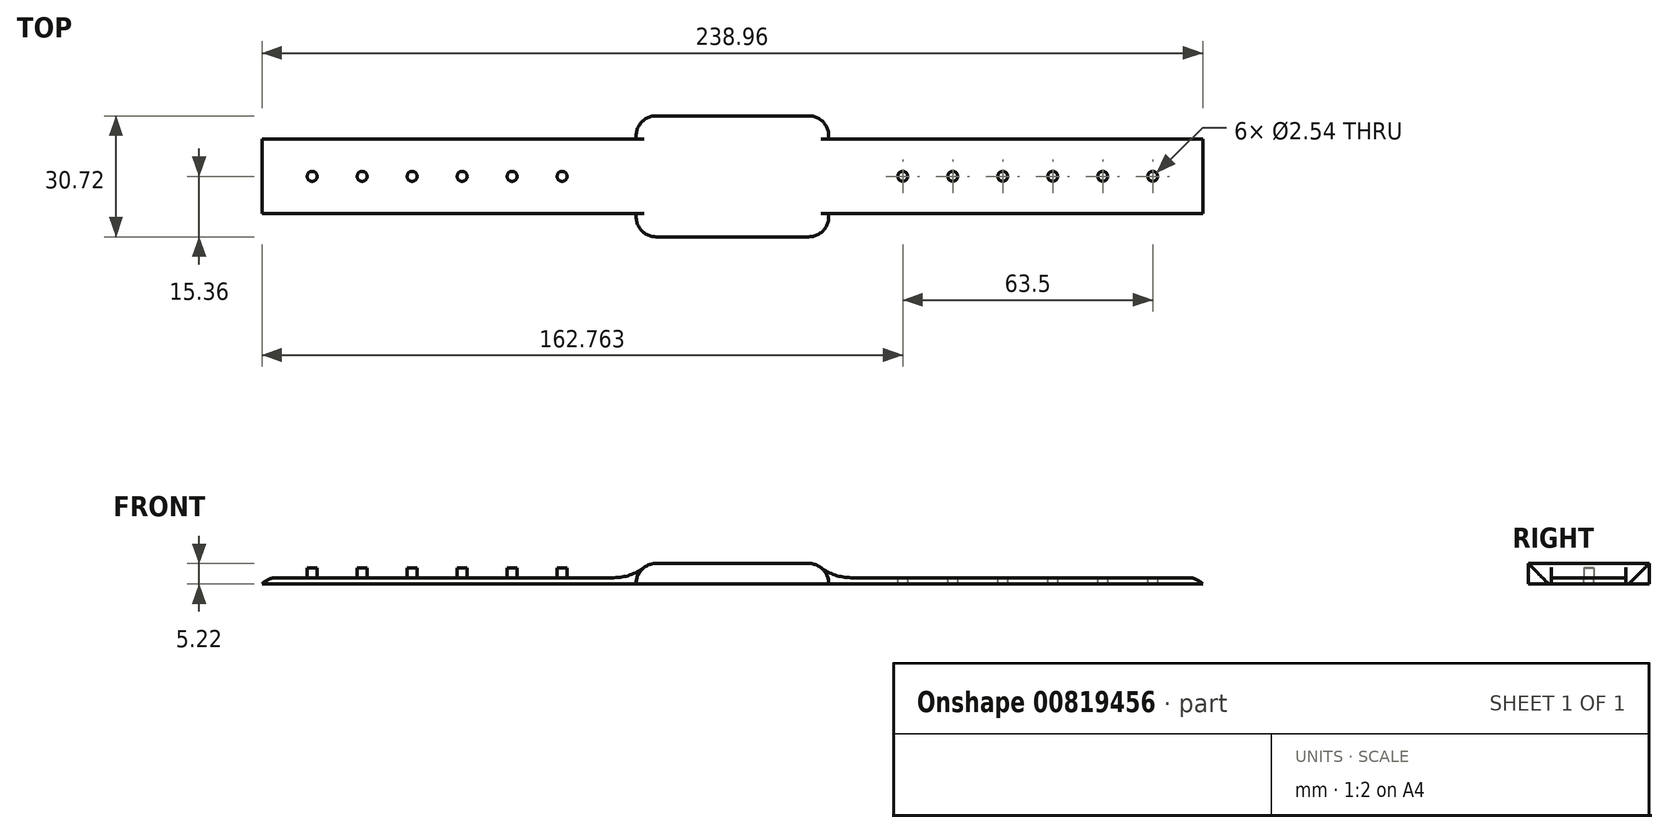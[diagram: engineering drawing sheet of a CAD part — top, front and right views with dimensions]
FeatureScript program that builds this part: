
annotation { "Feature Type Name" : "Feature", "Feature Type Description" : "" }
export const myFeature = defineFeature(function(context is Context, id is Id, definition is map)
    precondition{}
    {
        {
            var Q0;
            Q0=qCreatedBy(makeId("Top.planeOp"),FACE);
            var sketch = newSketch(context, id + "F0", { "sketchPlane" : qUnion([Q0])});
            skLineSegment(sketch, "E0.bottom", {"start": v(24.46, -15.36) * mm, "end": v(-24.46, -15.36) * mm});
            skLineSegment(sketch, "E0.top", {"start": v(24.46, 15.36) * mm, "end": v(-24.46, 15.36) * mm});
            skLineSegment(sketch, "E0.left", {"start": v(24.46, -15.36) * mm, "end": v(24.46, 15.36) * mm});
            skLineSegment(sketch, "E0.right", {"start": v(-24.46, -15.36) * mm, "end": v(-24.46, 15.36) * mm});
            skPoint(sketch, "E0.middle", {"position": v(0, 0) * mm});
            skLineSegment(sketch, "E1.bottom", {"start": v(-24.46, -9.45) * mm, "end": v(-119.48, -9.45) * mm});
            skLineSegment(sketch, "E1.top", {"start": v(-24.46, 9.45) * mm, "end": v(-119.48, 9.45) * mm});
            skLineSegment(sketch, "E1.left", {"start": v(-24.46, -9.45) * mm, "end": v(-24.46, 9.45) * mm});
            skLineSegment(sketch, "E1.right", {"start": v(-119.48, -9.45) * mm, "end": v(-119.48, 9.45) * mm});
            skLineSegment(sketch, "E2.MirrorCS", {"start": v(24.46, 9.45) * mm, "end": v(119.48, 9.45) * mm});
            skLineSegment(sketch, "E3.MirrorCS", {"start": v(119.48, -9.45) * mm, "end": v(119.48, 9.45) * mm});
            skLineSegment(sketch, "E4.MirrorCS", {"start": v(24.46, -9.45) * mm, "end": v(119.48, -9.45) * mm});
            skSolve(sketch);
        }
        {
            var Q0;
            Q0 = qSketchRegion(id + "F0", true);
            extrude(context, id + "F1", {"entities" : qUnion([Q0]), "depth" : 1.6 * mm, "offsetDistance" : 25.4 * mm});
        }
        {
            var Q0;
            Q0=makeQuery(id+"F1.opExtrude","CAP_FACE",FACE,{"disambiguationData":[OSD([sQuery(id+"F0.wireOp",EDGE,"E0.bottom"),sQuery(id+"F0.wireOp",EDGE,"E0.top"),sQuery(id+"F0.wireOp",EDGE,"E0.left"),sQuery(id+"F0.wireOp",EDGE,"E0.right"),sQuery(id+"F0.wireOp",EDGE,"E1.bottom"),sQuery(id+"F0.wireOp",EDGE,"E1.top"),sQuery(id+"F0.wireOp",EDGE,"E1.right"),sQuery(id+"F0.wireOp",EDGE,"E2.MirrorCS"),sQuery(id+"F0.wireOp",EDGE,"E3.MirrorCS"),sQuery(id+"F0.wireOp",EDGE,"E4.MirrorCS")])],"isStart":false});
            var sketch = newSketch(context, id + "F2", { "sketchPlane" : qUnion([Q0])});
            skLineSegment(sketch, "E5", {"start": v(119.48, 0) * mm, "end": v(106.78, 0) * mm, "construction": true});
            skLineSegment(sketch, "E6", {"start": v(106.78, 0) * mm, "end": v(94.08, 0) * mm, "construction": true});
            skLineSegment(sketch, "E7", {"start": v(94.08, 0) * mm, "end": v(81.38, 0) * mm, "construction": true});
            skLineSegment(sketch, "E8", {"start": v(81.38, 0) * mm, "end": v(68.68, 0) * mm, "construction": true});
            skLineSegment(sketch, "E9", {"start": v(68.68, 0) * mm, "end": v(55.98, 0) * mm, "construction": true});
            skLineSegment(sketch, "E10", {"start": v(55.98, 0) * mm, "end": v(43.28, 0) * mm, "construction": true});
            skCircle(sketch, "E11", {"center": v(106.78, 0) * mm, "radius": 1.27 * mm});
            skCircle(sketch, "E12", {"center": v(94.08, 0) * mm, "radius": 1.27 * mm});
            skCircle(sketch, "E13", {"center": v(81.38, 0) * mm, "radius": 1.27 * mm});
            skCircle(sketch, "E14", {"center": v(68.68, 0) * mm, "radius": 1.27 * mm});
            skCircle(sketch, "E15", {"center": v(55.98, 0) * mm, "radius": 1.27 * mm});
            skCircle(sketch, "E16", {"center": v(43.28, 0) * mm, "radius": 1.27 * mm});
            skSolve(sketch);
        }
        {
            var Q0;
            Q0 = qSketchRegion(id + "F2", true);
            extrude(context, id + "F3", {"entities" : qUnion([Q0]), "operationType" : NewBodyOperationType.REMOVE, "oppositeDirection" : true, "depth" : 25.4 * mm, "offsetDistance" : 25.4 * mm});
        }
        {
            var Q0;
            Q0=makeQuery(id+"F2.imprint","IMPRINT",FACE,{"disambiguationData":[TD([[makeQuery(id+"F2.imprint","IMPRINT",EDGE,{"derivedFrom":sQuery(id+"F2.wireOp",EDGE,"E11")}),-1.0]])]});
            var sketch = newSketch(context, id + "F4", { "sketchPlane" : qUnion([Q0])});
            skLineSegment(sketch, "E17", {"start": v(-119.47, 0) * mm, "end": v(-106.77, 0) * mm, "construction": true});
            skLineSegment(sketch, "E18", {"start": v(-106.77, 0) * mm, "end": v(-94.07, 0) * mm, "construction": true});
            skLineSegment(sketch, "E19", {"start": v(-94.07, 0) * mm, "end": v(-81.37, 0) * mm, "construction": true});
            skLineSegment(sketch, "E20", {"start": v(-81.37, 0) * mm, "end": v(-68.67, 0) * mm, "construction": true});
            skLineSegment(sketch, "E21", {"start": v(-68.67, 0) * mm, "end": v(-55.97, 0) * mm, "construction": true});
            skLineSegment(sketch, "E22", {"start": v(-55.97, 0) * mm, "end": v(-43.27, 0) * mm, "construction": true});
            skCircle(sketch, "E23", {"center": v(-106.77, 0) * mm, "radius": 1.27 * mm});
            skCircle(sketch, "E24", {"center": v(-94.07, 0) * mm, "radius": 1.27 * mm});
            skCircle(sketch, "E25", {"center": v(-81.37, 0) * mm, "radius": 1.27 * mm});
            skCircle(sketch, "E26", {"center": v(-68.67, 0) * mm, "radius": 1.27 * mm});
            skCircle(sketch, "E27", {"center": v(-55.97, 0) * mm, "radius": 1.27 * mm});
            skCircle(sketch, "E28", {"center": v(-43.27, 0) * mm, "radius": 1.27 * mm});
            skSolve(sketch);
        }
        {
            var Q0;
            Q0 = qSketchRegion(id + "F4", true);
            extrude(context, id + "F5", {"entities" : qUnion([Q0]), "operationType" : NewBodyOperationType.ADD, "depth" : 2.54 * mm, "offsetDistance" : 25.4 * mm});
        }
        {
            var Q0;
            Q0=makeQuery(id+"F1.opExtrude","CAP_FACE",FACE,{"disambiguationData":[OSD([sQuery(id+"F0.wireOp",EDGE,"E0.bottom"),sQuery(id+"F0.wireOp",EDGE,"E0.top"),sQuery(id+"F0.wireOp",EDGE,"E0.left"),sQuery(id+"F0.wireOp",EDGE,"E0.right"),sQuery(id+"F0.wireOp",EDGE,"E1.bottom"),sQuery(id+"F0.wireOp",EDGE,"E1.top"),sQuery(id+"F0.wireOp",EDGE,"E1.right"),sQuery(id+"F0.wireOp",EDGE,"E2.MirrorCS"),sQuery(id+"F0.wireOp",EDGE,"E3.MirrorCS"),sQuery(id+"F0.wireOp",EDGE,"E4.MirrorCS")])],"isStart":false});
            var sketch = newSketch(context, id + "F6", { "sketchPlane" : qUnion([Q0])});
            skLineSegment(sketch, "E29.bottom", {"start": v(-24.46, 15.36) * mm, "end": v(24.46, 15.36) * mm});
            skLineSegment(sketch, "E29.top", {"start": v(-24.46, -15.36) * mm, "end": v(24.46, -15.36) * mm});
            skLineSegment(sketch, "E29.left", {"start": v(-24.46, 15.36) * mm, "end": v(-24.46, -15.36) * mm});
            skLineSegment(sketch, "E29.right", {"start": v(24.46, 15.36) * mm, "end": v(24.46, -15.36) * mm});
            skSolve(sketch);
        }
        {
            var Q0;
            Q0 = qSketchRegion(id + "F6", true);
            extrude(context, id + "F7", {"entities" : qUnion([Q0]), "operationType" : NewBodyOperationType.ADD, "depth" : 3.62 * mm, "offsetDistance" : 25.4 * mm});
        }
        {
            var Q0;
            Q0=makeQuery(id+"F7.opExtrude","CAP_EDGE",EDGE,{"disambiguationData":[OSD([sQuery(id+"F6.wireOp",EDGE,"E29.right")])],"isStart":false});
            var Q1;
            Q1=makeQuery(id+"F7.opExtrude","CAP_EDGE",EDGE,{"disambiguationData":[OSD([sQuery(id+"F6.wireOp",EDGE,"E29.left")])],"isStart":false});
            var Q2;
            Q2=makeQuery(id+"F7.boolean.opBoolean","MERGE",EDGE,{"derivedFrom":[makeQuery(id+"F1.opExtrude","SWEPT_EDGE",EDGE,{"disambiguationData":[OSD([sQuery(id+"F0.wireOp",EDGE,"E0.top"),sQuery(id+"F0.wireOp",EDGE,"E0.right")])]}),makeQuery(id+"F7.opExtrude","SWEPT_EDGE",EDGE,{"disambiguationData":[OSD([sQuery(id+"F6.wireOp",EDGE,"E29.bottom"),sQuery(id+"F6.wireOp",EDGE,"E29.left")])]})]});
            var Q3;
            Q3=makeQuery(id+"F7.boolean.opBoolean","MERGE",EDGE,{"derivedFrom":[makeQuery(id+"F1.opExtrude","SWEPT_EDGE",EDGE,{"disambiguationData":[OSD([sQuery(id+"F0.wireOp",EDGE,"E0.bottom"),sQuery(id+"F0.wireOp",EDGE,"E0.right")])]}),makeQuery(id+"F7.opExtrude","SWEPT_EDGE",EDGE,{"disambiguationData":[OSD([sQuery(id+"F6.wireOp",EDGE,"E29.top"),sQuery(id+"F6.wireOp",EDGE,"E29.left")])]})]});
            var Q4;
            Q4=makeQuery(id+"F7.boolean.opBoolean","MERGE",EDGE,{"derivedFrom":[makeQuery(id+"F1.opExtrude","SWEPT_EDGE",EDGE,{"disambiguationData":[OSD([sQuery(id+"F0.wireOp",EDGE,"E0.bottom"),sQuery(id+"F0.wireOp",EDGE,"E0.left")])]}),makeQuery(id+"F7.opExtrude","SWEPT_EDGE",EDGE,{"disambiguationData":[OSD([sQuery(id+"F6.wireOp",EDGE,"E29.top"),sQuery(id+"F6.wireOp",EDGE,"E29.right")])]})]});
            var Q5;
            Q5=makeQuery(id+"F7.boolean.opBoolean","MERGE",EDGE,{"derivedFrom":[makeQuery(id+"F1.opExtrude","SWEPT_EDGE",EDGE,{"disambiguationData":[OSD([sQuery(id+"F0.wireOp",EDGE,"E0.top"),sQuery(id+"F0.wireOp",EDGE,"E0.left")])]}),makeQuery(id+"F7.opExtrude","SWEPT_EDGE",EDGE,{"disambiguationData":[OSD([sQuery(id+"F6.wireOp",EDGE,"E29.bottom"),sQuery(id+"F6.wireOp",EDGE,"E29.right")])]})]});
            fillet(context, id + "F8", {"entities" : qUnion([Q0, Q1, Q2, Q3, Q4, Q5]), "radius" : 5.08 * mm, "tangentPropagation" : true, "allowEdgeOverflow" : false});
        }
        {
            var Q0;
            Q0=makeQuery(id+"F1.opExtrude","CAP_EDGE",EDGE,{"disambiguationData":[OSD([sQuery(id+"F0.wireOp",EDGE,"E3.MirrorCS")])],"isStart":false});
            var Q1;
            Q1=makeQuery(id+"F1.opExtrude","CAP_EDGE",EDGE,{"disambiguationData":[OSD([sQuery(id+"F0.wireOp",EDGE,"E1.right")])],"isStart":false});
            fillet(context, id + "F9", {"entities" : qUnion([Q0, Q1]), "radius" : 5.08 * mm, "tangentPropagation" : true, "allowEdgeOverflow" : false});
        }
        {
            var Q0;
            {var subQ0=sQuery(id+"F0.wireOp",EDGE,"E4.MirrorCS");var subQ1=sQuery(id+"F0.wireOp",EDGE,"E0.left");var subQ2=sQuery(id+"F0.wireOp",EDGE,"E0.bottom");var subQ3=sQuery(id+"F0.wireOp",EDGE,"E0.top");var subQ4=sQuery(id+"F0.wireOp",EDGE,"E2.MirrorCS");var subQ5=sQuery(id+"F0.wireOp",EDGE,"E3.MirrorCS");var subQ6=sQuery(id+"F6.wireOp",EDGE,"E29.right");Q0=makeQuery(id+"F8.opFillet","BLEND_EDGE",EDGE,{"blendedFrom":[makeQuery(id+"F7.opExtrude","CAP_EDGE",EDGE,{"disambiguationData":[OSD([subQ6])],"isStart":false}),makeQuery(id+"F7.boolean.opBoolean","SPLIT",FACE,{"disambiguationData":[TD([makeQuery(id+"F1.opExtrude","SWEPT_FACE",FACE,{"disambiguationData":[OSD([subQ4])]})])],"derivedFrom":makeQuery(id+"F1.opExtrude","CAP_FACE",FACE,{"disambiguationData":[OSD([subQ2,subQ3,subQ1,sQuery(id+"F0.wireOp",EDGE,"E0.right"),sQuery(id+"F0.wireOp",EDGE,"E1.bottom"),sQuery(id+"F0.wireOp",EDGE,"E1.top"),sQuery(id+"F0.wireOp",EDGE,"E1.right"),subQ4,subQ5,subQ0])],"isStart":false})})],"blendedInto":[makeQuery(id+"F7.boolean.opBoolean","SPLIT",FACE,{"disambiguationData":[TD([makeQuery(id+"F1.opExtrude","SWEPT_FACE",FACE,{"disambiguationData":[OSD([subQ4])]})])],"derivedFrom":makeQuery(id+"F1.opExtrude","CAP_FACE",FACE,{"disambiguationData":[OSD([subQ2,subQ3,subQ1,sQuery(id+"F0.wireOp",EDGE,"E0.right"),sQuery(id+"F0.wireOp",EDGE,"E1.bottom"),sQuery(id+"F0.wireOp",EDGE,"E1.top"),sQuery(id+"F0.wireOp",EDGE,"E1.right"),subQ4,subQ5,subQ0])],"isStart":false})})]});}
            var Q1;
            {var subQ0=sQuery(id+"F0.wireOp",EDGE,"E1.right");var subQ1=sQuery(id+"F0.wireOp",EDGE,"E0.right");var subQ2=sQuery(id+"F0.wireOp",EDGE,"E0.bottom");var subQ4=sQuery(id+"F0.wireOp",EDGE,"E1.bottom");var subQ5=sQuery(id+"F0.wireOp",EDGE,"E0.top");var subQ6=sQuery(id+"F0.wireOp",EDGE,"E1.top");var subQ7=sQuery(id+"F6.wireOp",EDGE,"E29.left");Q1=makeQuery(id+"F8.opFillet","BLEND_EDGE",EDGE,{"blendedFrom":[makeQuery(id+"F7.opExtrude","CAP_EDGE",EDGE,{"disambiguationData":[OSD([subQ7])],"isStart":false}),makeQuery(id+"F7.boolean.opBoolean","SPLIT",FACE,{"disambiguationData":[TD([makeQuery(id+"F1.opExtrude","SWEPT_FACE",FACE,{"disambiguationData":[OSD([subQ4])]})])],"derivedFrom":makeQuery(id+"F1.opExtrude","CAP_FACE",FACE,{"disambiguationData":[OSD([subQ2,subQ5,sQuery(id+"F0.wireOp",EDGE,"E0.left"),subQ1,subQ4,subQ6,subQ0,sQuery(id+"F0.wireOp",EDGE,"E2.MirrorCS"),sQuery(id+"F0.wireOp",EDGE,"E3.MirrorCS"),sQuery(id+"F0.wireOp",EDGE,"E4.MirrorCS")])],"isStart":false})})],"blendedInto":[makeQuery(id+"F7.boolean.opBoolean","SPLIT",FACE,{"disambiguationData":[TD([makeQuery(id+"F1.opExtrude","SWEPT_FACE",FACE,{"disambiguationData":[OSD([subQ4])]})])],"derivedFrom":makeQuery(id+"F1.opExtrude","CAP_FACE",FACE,{"disambiguationData":[OSD([subQ2,subQ5,sQuery(id+"F0.wireOp",EDGE,"E0.left"),subQ1,subQ4,subQ6,subQ0,sQuery(id+"F0.wireOp",EDGE,"E2.MirrorCS"),sQuery(id+"F0.wireOp",EDGE,"E3.MirrorCS"),sQuery(id+"F0.wireOp",EDGE,"E4.MirrorCS")])],"isStart":false})})]});}
            fillet(context, id + "F10", {"entities" : qUnion([Q0, Q1]), "radius" : 12.7 * mm, "tangentPropagation" : true, "allowEdgeOverflow" : false});
        }
    });
